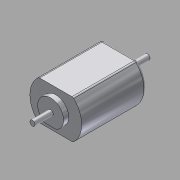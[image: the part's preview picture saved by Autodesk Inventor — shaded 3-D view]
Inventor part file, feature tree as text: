
AUTODESK INVENTOR PART (.ipt)
format: ipt  version: 2015 (Build 190159000, 159)  size: 138,752 bytes
history: native  units: in
note: dims shown in document units (in); Inventor stores cm internally (conversion verified against a paired STEP export)
features: sketch x5, other x3
ambient origin geometry x8: Origin, YZ Plane, XZ Plane, XY Plane, X Axis, Y Axis, Z Axis, Center Point
bodies: Solid1 (feature_tree)
feature tree (8):
  other  "motor_MIR1.ipt"
  other  "Solid1::motor_MIR1.ipt"
  other  "TaggingFeature1"
  sketch  "Sketch1"  dims[d0=0.3937in]
  sketch  "Sketch2"
  sketch  "Sketch3"
  sketch  "Sketch4"
  sketch  "Sketch5"
